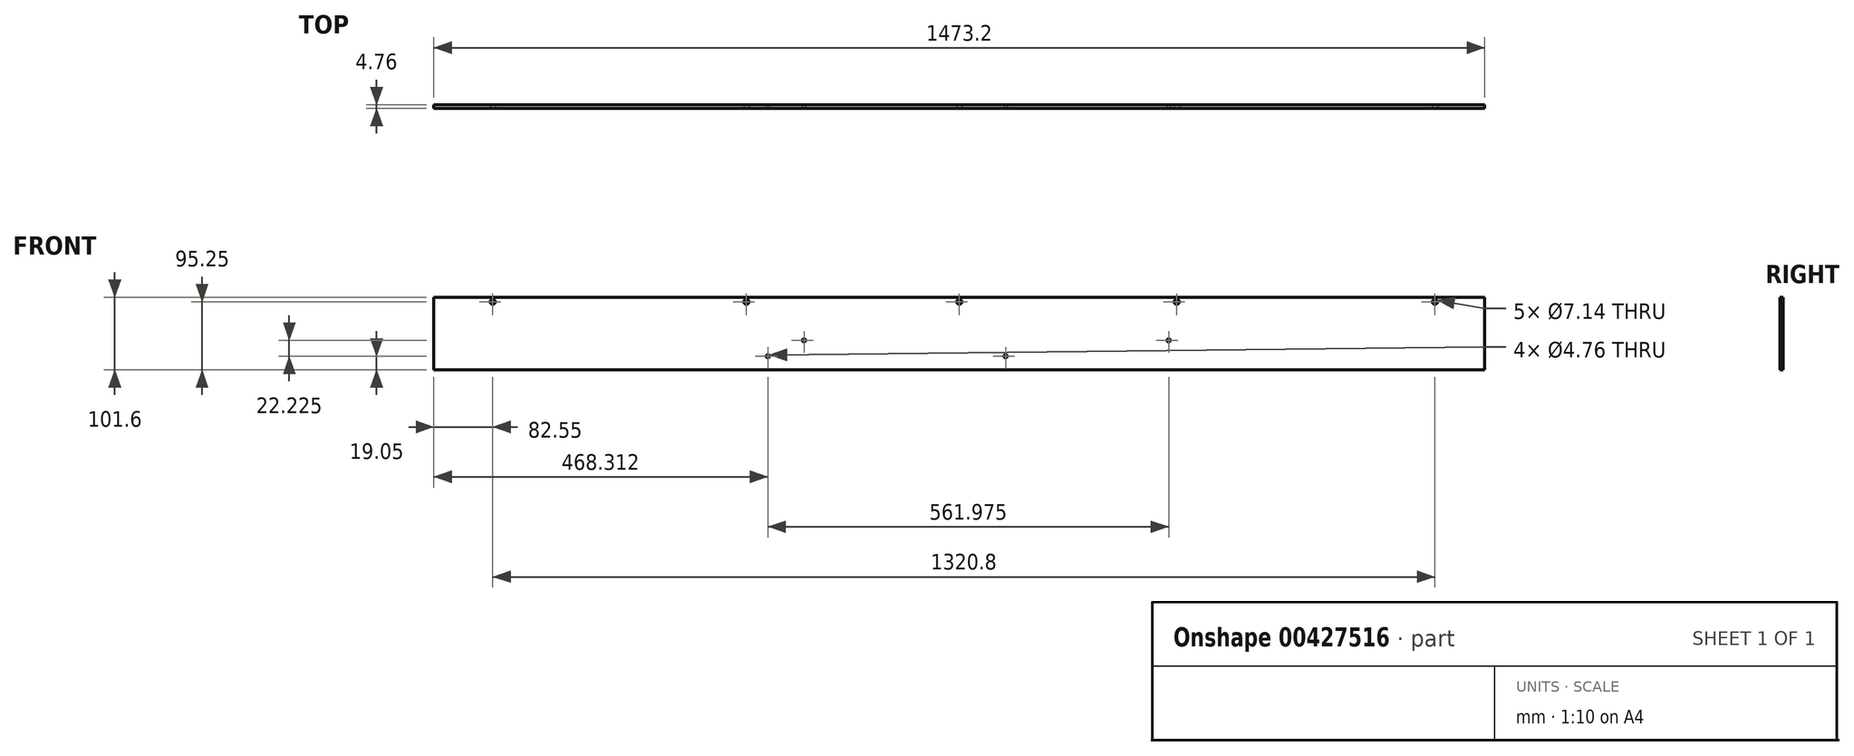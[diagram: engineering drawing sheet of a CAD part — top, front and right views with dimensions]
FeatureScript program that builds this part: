
annotation { "Feature Type Name" : "Feature", "Feature Type Description" : "" }
export const myFeature = defineFeature(function(context is Context, id is Id, definition is map)
    precondition{}
    {
        {
            var Q0;
            Q0=qCreatedBy(makeId("Front.planeOp"),FACE);
            var sketch = newSketch(context, id + "F0", { "sketchPlane" : qUnion([Q0])});
            skLineSegment(sketch, "E0.bottom", {"start": v(0, 0) * mm, "end": v(1473.2, 0) * mm});
            skLineSegment(sketch, "E0.top", {"start": v(0, 101.6) * mm, "end": v(1473.2, 101.6) * mm});
            skLineSegment(sketch, "E0.left", {"start": v(0, 0) * mm, "end": v(0, 101.6) * mm});
            skLineSegment(sketch, "E0.right", {"start": v(1473.2, 0) * mm, "end": v(1473.2, 101.6) * mm});
            skSolve(sketch);
        }
        {
            var Q0;
            Q0=makeQuery(id+"F0.imprint","IMPRINT",FACE,{"disambiguationData":[TD([[makeQuery(id+"F0.imprint","IMPRINT",EDGE,{"derivedFrom":sQuery(id+"F0.wireOp",EDGE,"E0.bottom")}),1.0]])]});
            extrude(context, id + "F1", {"entities" : qUnion([Q0]), "oppositeDirection" : true, "depth" : 4.76 * mm});
        }
        {
            var Q0;
            Q0=makeQuery(id+"F1.opExtrude","CAP_FACE",FACE,{"disambiguationData":[OSD([sQuery(id+"F0.wireOp",EDGE,"E0.bottom"),sQuery(id+"F0.wireOp",EDGE,"E0.top"),sQuery(id+"F0.wireOp",EDGE,"E0.left"),sQuery(id+"F0.wireOp",EDGE,"E0.right")])],"isStart":true});
            var sketch = newSketch(context, id + "F2", { "sketchPlane" : qUnion([Q0])});
            skCircle(sketch, "E1", {"center": v(82.55, 95.25) * mm, "radius": 3.57 * mm});
            skCircle(sketch, "E2", {"center": v(438.15, 95.25) * mm, "radius": 3.57 * mm});
            skCircle(sketch, "E3", {"center": v(736.6, 95.25) * mm, "radius": 3.57 * mm});
            skCircle(sketch, "E4", {"center": v(1041.4, 95.25) * mm, "radius": 3.57 * mm});
            skCircle(sketch, "E5", {"center": v(1403.35, 95.25) * mm, "radius": 3.57 * mm});
            skSolve(sketch);
        }
        {
            var Q0;
            Q0=makeQuery(id+"F2.imprint","IMPRINT",FACE,{"disambiguationData":[TD([[makeQuery(id+"F2.imprint","IMPRINT",EDGE,{"derivedFrom":sQuery(id+"F2.wireOp",EDGE,"E1")}),1.0]])]});
            var Q1;
            Q1=makeQuery(id+"F2.imprint","IMPRINT",FACE,{"disambiguationData":[TD([[makeQuery(id+"F2.imprint","IMPRINT",EDGE,{"derivedFrom":sQuery(id+"F2.wireOp",EDGE,"E2")}),1.0]])]});
            var Q2;
            Q2=makeQuery(id+"F2.imprint","IMPRINT",FACE,{"disambiguationData":[TD([[makeQuery(id+"F2.imprint","IMPRINT",EDGE,{"derivedFrom":sQuery(id+"F2.wireOp",EDGE,"E3")}),1.0]])]});
            var Q3;
            Q3=makeQuery(id+"F2.imprint","IMPRINT",FACE,{"disambiguationData":[TD([[makeQuery(id+"F2.imprint","IMPRINT",EDGE,{"derivedFrom":sQuery(id+"F2.wireOp",EDGE,"E4")}),1.0]])]});
            var Q4;
            Q4=makeQuery(id+"F2.imprint","IMPRINT",FACE,{"disambiguationData":[TD([[makeQuery(id+"F2.imprint","IMPRINT",EDGE,{"derivedFrom":sQuery(id+"F2.wireOp",EDGE,"E5")}),1.0]])]});
            extrude(context, id + "F3", {"entities" : qUnion([Q0, Q1, Q2, Q3, Q4]), "operationType" : NewBodyOperationType.REMOVE, "endBound" : BoundingType.THROUGH_ALL, "oppositeDirection" : true, "depth" : 25.4 * mm});
        }
        {
            var Q0;
            Q0=makeQuery(id+"F1.opExtrude","CAP_FACE",FACE,{"disambiguationData":[OSD([sQuery(id+"F0.wireOp",EDGE,"E0.bottom"),sQuery(id+"F0.wireOp",EDGE,"E0.top"),sQuery(id+"F0.wireOp",EDGE,"E0.left"),sQuery(id+"F0.wireOp",EDGE,"E0.right")])],"isStart":true});
            var sketch = newSketch(context, id + "F4", { "sketchPlane" : qUnion([Q0])});
            skCircle(sketch, "E6", {"center": v(519.11, 41.28) * mm, "radius": 2.38 * mm});
            skCircle(sketch, "E7", {"center": v(1030.29, 41.28) * mm, "radius": 2.38 * mm});
            skSolve(sketch);
        }
        {
            var Q0;
            Q0=makeQuery(id+"F4.imprint","IMPRINT",FACE,{"disambiguationData":[TD([[makeQuery(id+"F4.imprint","IMPRINT",EDGE,{"derivedFrom":sQuery(id+"F4.wireOp",EDGE,"E6")}),1.0]])]});
            var Q1;
            Q1=makeQuery(id+"F4.imprint","IMPRINT",FACE,{"disambiguationData":[TD([[makeQuery(id+"F4.imprint","IMPRINT",EDGE,{"derivedFrom":sQuery(id+"F4.wireOp",EDGE,"E7")}),1.0]])]});
            extrude(context, id + "F5", {"entities" : qUnion([Q0, Q1]), "operationType" : NewBodyOperationType.REMOVE, "endBound" : BoundingType.THROUGH_ALL, "oppositeDirection" : true, "depth" : 25.4 * mm});
        }
        {
            var Q0;
            Q0=makeQuery(id+"F1.opExtrude","CAP_FACE",FACE,{"disambiguationData":[OSD([sQuery(id+"F0.wireOp",EDGE,"E0.bottom"),sQuery(id+"F0.wireOp",EDGE,"E0.top"),sQuery(id+"F0.wireOp",EDGE,"E0.left"),sQuery(id+"F0.wireOp",EDGE,"E0.right")])],"isStart":true});
            var sketch = newSketch(context, id + "F6", { "sketchPlane" : qUnion([Q0])});
            skCircle(sketch, "E8", {"center": v(468.31, 19.05) * mm, "radius": 2.38 * mm});
            skCircle(sketch, "E9", {"center": v(801.69, 19.05) * mm, "radius": 2.38 * mm});
            skSolve(sketch);
        }
        {
            var Q0;
            Q0=makeQuery(id+"F6.imprint","IMPRINT",FACE,{"disambiguationData":[TD([[makeQuery(id+"F6.imprint","IMPRINT",EDGE,{"derivedFrom":sQuery(id+"F6.wireOp",EDGE,"E8")}),1.0]])]});
            var Q1;
            Q1=makeQuery(id+"F6.imprint","IMPRINT",FACE,{"disambiguationData":[TD([[makeQuery(id+"F6.imprint","IMPRINT",EDGE,{"derivedFrom":sQuery(id+"F6.wireOp",EDGE,"E9")}),1.0]])]});
            extrude(context, id + "F7", {"entities" : qUnion([Q0, Q1]), "operationType" : NewBodyOperationType.REMOVE, "endBound" : BoundingType.THROUGH_ALL, "oppositeDirection" : true, "depth" : 25.4 * mm});
        }
    });
